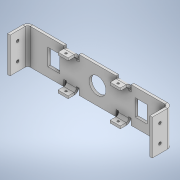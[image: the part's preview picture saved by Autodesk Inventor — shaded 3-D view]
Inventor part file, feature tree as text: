
AUTODESK INVENTOR PART (.ipt)
format: ipt  version: 2021 (Build 250183000, 183)  size: 335,360 bytes
history: native  units: mm
features: other x11, sketch x9, hole x4, sheet_metal_op x3, mirror x2
ambient origin geometry x8: Origin, YZ Plane, XZ Plane, XY Plane, X Axis, Y Axis, Z Axis, Center Point
bodies: Body1 (feature_tree)
feature tree (29):
  other  "Sólido1"
  sheet_metal_op  "Face1"
  sheet_metal_op  "Flange1"
  sheet_metal_op  "Flange2"
  mirror  "Espelhamento1"
  mirror  "Espelhamento2"
  hole  "Furo1"  [1 undecoded]
  hole  "Furo2"  [1 undecoded]
  hole  "Furo3"  [1 undecoded]
  hole  "Furo4"  [1 undecoded]
  sketch  "Esboço1"  dims[d0=172.0mm d1=42.0mm]
  other  "Placa1"
  sketch  "Esboço2"  dims[d2=3.0mm d3=3.0mm]
  other  "Placa2"
  other  "Vergadura1"
  other  "Canto1"
  sketch  "Esboço3"  dims[d4=1.5mm d5=6.0mm]
  sketch  "Esboço4"  dims[d6=3.0mm d7=21.0mm d8=90.0deg d9=3.0mm]
  other  "Placa3"
  other  "Vergadura2"
  other  "Canto2"
  sketch  "Esboço5"  dims[d10=12.0mm]
  sketch  "Esboço6"  dims[d11=3.0mm]
  sketch  "Esboço7"  dims[d12=3.0mm]
  sketch  "Esboço8"  dims[d13=180.0deg]
  sketch  "Esboço9"  dims[d15=18.0mm d16=3.0mm d17=3.0mm d18=0.0mm d19=3.0mm d20=1.5mm d21=6.0mm d22=3.0mm d23=10.0mm d24=90.0deg d25=3.0mm d26=12.0mm d27=3.0mm d28=3.0mm d29=14.0mm d30=20.0mm d31=3.0mm d32=0.0mm d33=5.0mm d34=20.0mm d35=6.0mm d36=4.0mm d37=2.0mm d38=90.0deg d39=3.0mm d40=20.594885mm d41=3.5mm d42=6.0mm d43=2.459mm d44=42.0mm d45=4.0mm d46=2.0mm d47=90.0deg d48=3.0mm d49=0.0mm d50=3.5mm d51=6.0mm d52=2.459mm d53=42.0mm d54=4.0mm d55=2.0mm d56=90.0deg d57=3.0mm d58=0.0mm d59=3.242mm d60=172.0mm d61=4.0mm d62=2.0mm d63=90.0deg d64=3.0mm d65=0.0mm]
  other  "Recortar1"
  other  "Recortar2"
  other  "Definição1"
note: 4 required parameter values undecoded (feature->parameter linkage not recoverable at this tier; creation-order binding heuristic only, values carry confidence <= 0.55)
